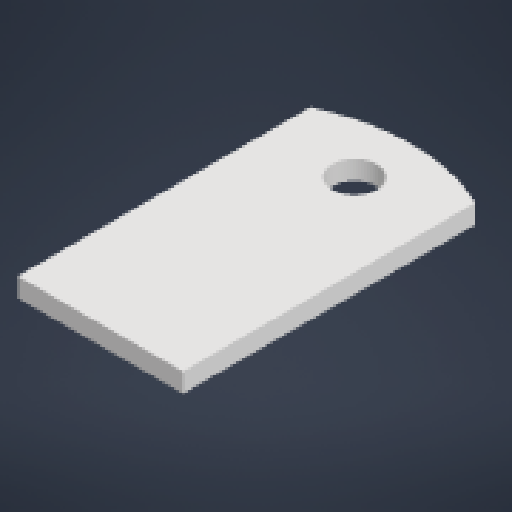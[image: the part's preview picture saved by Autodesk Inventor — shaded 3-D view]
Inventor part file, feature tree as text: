
AUTODESK INVENTOR PART (.ipt)
format: ipt  version: 2024 (Build 280153000, 153)  size: 149,504 bytes
history: native  units: mm
features: reference x12, other x5, extrude x2, sketch x2
ambient origin geometry x8: Origin, YZ Plane, XZ Plane, XY Plane, X Axis, Y Axis, Z Axis, Center Point
bodies: Body1 (feature_tree)
feature tree (21):
  other  "Твердое тело1"
  extrude  "Выдавливание1"  Depth=3.0mm TaperAngle=0.0deg
  extrude  "Выдавливание2"  Depth=3.0mm TaperAngle=0.0deg
  sketch  "Эскиз1"
  reference  "Ссылка1"
  reference  "Ссылка2"
  reference  "Ссылка3"
  reference  "Ссылка4"
  reference  "Ссылка5"
  sketch  "Эскиз3"
  reference  "Ссылка6"
  reference  "Ссылка8"
  reference  "Ссылка9"
  reference  "Ссылка10"
  reference  "Ссылка11"
  reference  "Ссылка12"
  reference  "Ссылка13"
  parser-record x1  (decoder bookkeeping rows leaked as tree rows — omitted from the tree; the rows remain in map.json)
  other  "arm_holder.iam"
  other  "arm_holder:1"
  other  "gasket_1:1"
note: 1 file-system path scrubbed to <path> (originals preserved in map.json)
